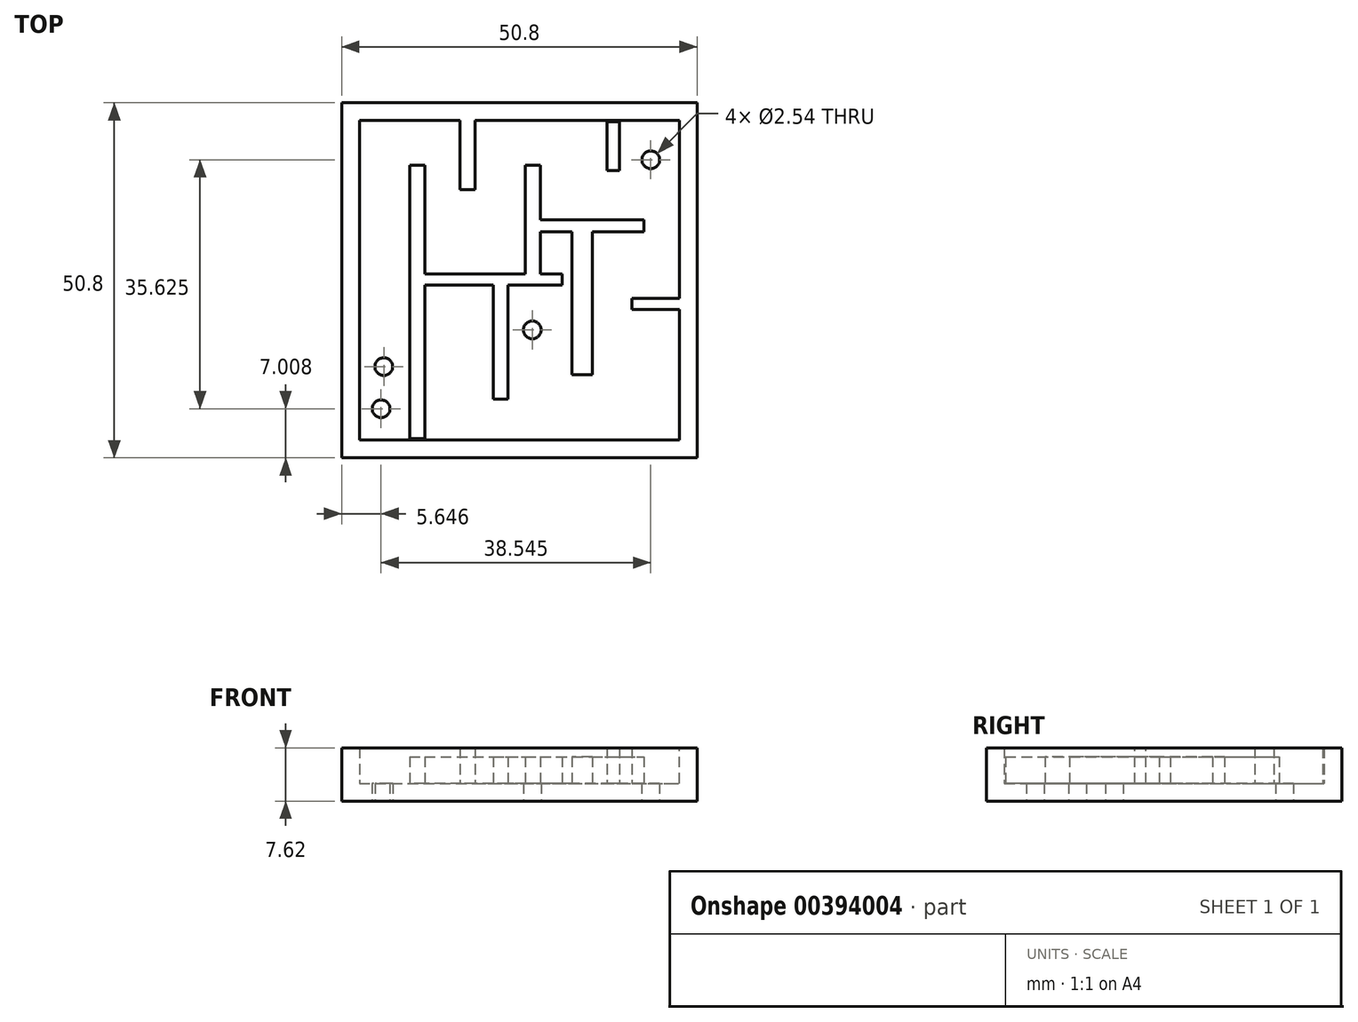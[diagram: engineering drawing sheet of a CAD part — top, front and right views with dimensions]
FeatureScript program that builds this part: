
annotation { "Feature Type Name" : "Feature", "Feature Type Description" : "" }
export const myFeature = defineFeature(function(context is Context, id is Id, definition is map)
    precondition{}
    {
        {
            var Q0;
            Q0=qCreatedBy(makeId("Top.planeOp"),FACE);
            var sketch = newSketch(context, id + "F0", { "sketchPlane" : qUnion([Q0])});
            skLineSegment(sketch, "E0.bottom", {"start": v(0, 0) * mm, "end": v(50.8, 0) * mm});
            skLineSegment(sketch, "E0.top", {"start": v(0, 50.8) * mm, "end": v(50.8, 50.8) * mm});
            skLineSegment(sketch, "E0.left", {"start": v(0, 0) * mm, "end": v(0, 50.8) * mm});
            skLineSegment(sketch, "E0.right", {"start": v(50.8, 0) * mm, "end": v(50.8, 50.8) * mm});
            skSolve(sketch);
        }
        {
            var Q0;
            Q0 = qSketchRegion(id + "F0", true);
            extrude(context, id + "F1", {"entities" : qUnion([Q0]), "depth" : 7.62 * mm});
        }
        {
            var Q0;
            Q0=makeQuery(id+"F1.opExtrude","CAP_FACE",FACE,{"disambiguationData":[OSD([sQuery(id+"F0.wireOp",EDGE,"E0.bottom"),sQuery(id+"F0.wireOp",EDGE,"E0.top"),sQuery(id+"F0.wireOp",EDGE,"E0.left"),sQuery(id+"F0.wireOp",EDGE,"E0.right")])],"isStart":false});
            shell(context, id + "F2", {"entities" : qUnion([Q0]), "thickness" : 2.54 * mm});
        }
        {
            var Q0;
            Q0=qCreatedBy(makeId("Top.planeOp"),FACE);
            var sketch = newSketch(context, id + "F3", { "sketchPlane" : qUnion([Q0])});
            skLineSegment(sketch, "E1.bottom", {"start": v(9.73, 2.73) * mm, "end": v(11.87, 2.73) * mm});
            skLineSegment(sketch, "E1.top", {"start": v(9.73, 41.85) * mm, "end": v(11.87, 41.85) * mm});
            skLineSegment(sketch, "E1.left", {"start": v(9.73, 2.73) * mm, "end": v(9.73, 41.85) * mm});
            skLineSegment(sketch, "E1.right", {"start": v(11.87, 2.73) * mm, "end": v(11.87, 41.85) * mm});
            skLineSegment(sketch, "E2.bottom", {"start": v(11.87, 24.72) * mm, "end": v(31.54, 24.72) * mm});
            skLineSegment(sketch, "E2.top", {"start": v(11.87, 26.28) * mm, "end": v(31.54, 26.28) * mm});
            skLineSegment(sketch, "E2.left", {"start": v(11.87, 24.72) * mm, "end": v(11.87, 26.28) * mm});
            skLineSegment(sketch, "E2.right", {"start": v(31.54, 24.72) * mm, "end": v(31.54, 26.28) * mm});
            skLineSegment(sketch, "E3.bottom", {"start": v(21.7, 24.72) * mm, "end": v(23.75, 24.72) * mm});
            skLineSegment(sketch, "E3.top", {"start": v(21.7, 8.37) * mm, "end": v(23.75, 8.37) * mm});
            skLineSegment(sketch, "E3.left", {"start": v(21.7, 24.72) * mm, "end": v(21.7, 8.37) * mm});
            skLineSegment(sketch, "E3.right", {"start": v(23.75, 24.72) * mm, "end": v(23.75, 8.37) * mm});
            skLineSegment(sketch, "E4.bottom", {"start": v(26.28, 26.28) * mm, "end": v(28.42, 26.28) * mm});
            skLineSegment(sketch, "E4.top", {"start": v(26.28, 41.85) * mm, "end": v(28.42, 41.85) * mm});
            skLineSegment(sketch, "E4.left", {"start": v(26.28, 26.28) * mm, "end": v(26.28, 41.85) * mm});
            skLineSegment(sketch, "E4.right", {"start": v(28.42, 26.28) * mm, "end": v(28.42, 41.85) * mm});
            skLineSegment(sketch, "E5.bottom", {"start": v(28.42, 34.07) * mm, "end": v(43.22, 34.07) * mm});
            skLineSegment(sketch, "E5.top", {"start": v(28.42, 32.32) * mm, "end": v(43.22, 32.32) * mm});
            skLineSegment(sketch, "E5.left", {"start": v(28.42, 34.07) * mm, "end": v(28.42, 32.32) * mm});
            skLineSegment(sketch, "E5.right", {"start": v(43.22, 34.07) * mm, "end": v(43.22, 32.32) * mm});
            skLineSegment(sketch, "E6.bottom", {"start": v(35.82, 32.32) * mm, "end": v(32.9, 32.32) * mm});
            skLineSegment(sketch, "E6.top", {"start": v(35.82, 11.87) * mm, "end": v(32.9, 11.87) * mm});
            skLineSegment(sketch, "E6.left", {"start": v(35.82, 32.32) * mm, "end": v(35.82, 11.87) * mm});
            skLineSegment(sketch, "E6.right", {"start": v(32.9, 32.32) * mm, "end": v(32.9, 11.87) * mm});
            skPoint(sketch, "E7.oppositeSnap0", {"position": v(35.82, 22.1) * mm});
            skLineSegment(sketch, "E7.bottom", {"start": v(35.82, 22.1) * mm, "end": v(35.82, 22.1) * mm});
            skLineSegment(sketch, "E7.top", {"start": v(35.82, 24.72) * mm, "end": v(35.82, 24.72) * mm});
            skLineSegment(sketch, "E7.left", {"start": v(35.82, 22.1) * mm, "end": v(35.82, 24.72) * mm});
            skLineSegment(sketch, "E7.right", {"start": v(35.82, 22.1) * mm, "end": v(35.82, 24.72) * mm});
            skSolve(sketch);
        }
        {
            var Q0;
            Q0 = qSketchRegion(id + "F3", true);
            extrude(context, id + "F4", {"entities" : qUnion([Q0]), "operationType" : NewBodyOperationType.ADD, "depth" : 6.35 * mm});
        }
        {
            var Q0;
            Q0=qCreatedBy(makeId("Top.planeOp"),FACE);
            var sketch = newSketch(context, id + "F5", { "sketchPlane" : qUnion([Q0])});
            skLineSegment(sketch, "E8.bottom", {"start": v(16.94, 48.47) * mm, "end": v(19.08, 48.47) * mm});
            skLineSegment(sketch, "E8.top", {"start": v(16.94, 38.35) * mm, "end": v(19.08, 38.35) * mm});
            skLineSegment(sketch, "E8.left", {"start": v(16.94, 48.47) * mm, "end": v(16.94, 38.35) * mm});
            skLineSegment(sketch, "E8.right", {"start": v(19.08, 48.47) * mm, "end": v(19.08, 38.35) * mm});
            skLineSegment(sketch, "E9.bottom", {"start": v(48.28, 22.78) * mm, "end": v(41.47, 22.78) * mm});
            skLineSegment(sketch, "E9.top", {"start": v(48.28, 21.22) * mm, "end": v(41.47, 21.22) * mm});
            skLineSegment(sketch, "E9.left", {"start": v(48.28, 22.78) * mm, "end": v(48.28, 21.22) * mm});
            skLineSegment(sketch, "E9.right", {"start": v(41.47, 22.78) * mm, "end": v(41.47, 21.22) * mm});
            skSolve(sketch);
        }
        {
            var Q0;
            Q0 = qSketchRegion(id + "F5", true);
            extrude(context, id + "F6", {"entities" : qUnion([Q0]), "operationType" : NewBodyOperationType.ADD, "depth" : 7.62 * mm});
        }
        {
            var Q0;
            Q0=qCreatedBy(makeId("Top.planeOp"),FACE);
            var sketch = newSketch(context, id + "F7", { "sketchPlane" : qUnion([Q0])});
            skLineSegment(sketch, "E10.bottom", {"start": v(37.96, 48.08) * mm, "end": v(39.71, 48.08) * mm});
            skLineSegment(sketch, "E10.top", {"start": v(37.96, 41.08) * mm, "end": v(39.71, 41.08) * mm});
            skLineSegment(sketch, "E10.left", {"start": v(37.96, 48.08) * mm, "end": v(37.96, 41.08) * mm});
            skLineSegment(sketch, "E10.right", {"start": v(39.71, 48.08) * mm, "end": v(39.71, 41.08) * mm});
            skSolve(sketch);
        }
        {
            var Q0;
            Q0 = qSketchRegion(id + "F7", true);
            extrude(context, id + "F8", {"entities" : qUnion([Q0]), "operationType" : NewBodyOperationType.ADD, "depth" : 7.62 * mm});
        }
        {
            var Q0;
            Q0=qCreatedBy(makeId("Top.planeOp"),FACE);
            var sketch = newSketch(context, id + "F9", { "sketchPlane" : qUnion([Q0])});
            skCircle(sketch, "E11", {"center": v(5.65, 7) * mm, "radius": 1.27 * mm});
            skCircle(sketch, "E12", {"center": v(6.03, 13.04) * mm, "radius": 1.27 * mm});
            skCircle(sketch, "E13", {"center": v(44.2, 42.63) * mm, "radius": 1.27 * mm});
            skSolve(sketch);
        }
        {
            var Q0;
            Q0 = qSketchRegion(id + "F9", true);
            extrude(context, id + "F10", {"entities" : qUnion([Q0]), "operationType" : NewBodyOperationType.REMOVE, "depth" : 25.4 * mm});
        }
        {
            var Q0;
            Q0=qCreatedBy(makeId("Top.planeOp"),FACE);
            var sketch = newSketch(context, id + "F11", { "sketchPlane" : qUnion([Q0])});
            skCircle(sketch, "E14", {"center": v(27.25, 18.3) * mm, "radius": 1.27 * mm});
            skSolve(sketch);
        }
        {
            var Q0;
            Q0 = qSketchRegion(id + "F11", true);
            extrude(context, id + "F12", {"entities" : qUnion([Q0]), "operationType" : NewBodyOperationType.REMOVE, "depth" : 25.4 * mm});
        }
    });
